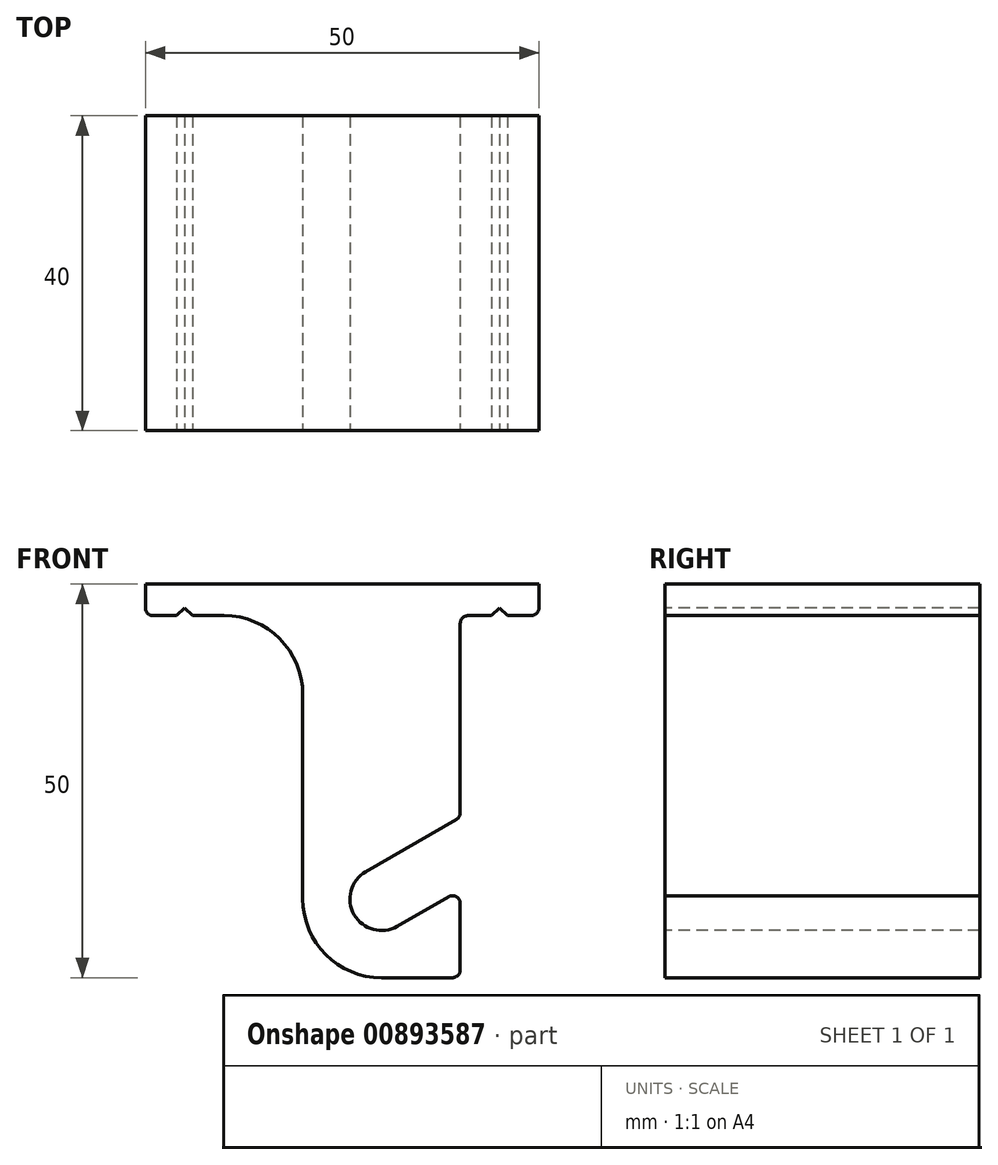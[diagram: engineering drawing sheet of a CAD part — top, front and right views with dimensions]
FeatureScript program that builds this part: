
annotation { "Feature Type Name" : "Feature", "Feature Type Description" : "" }
export const myFeature = defineFeature(function(context is Context, id is Id, definition is map)
    precondition{}
    {
        {
            var Q0;
            Q0=qCreatedBy(makeId("Front.planeOp"),FACE);
            var sketch = newSketch(context, id + "F0", { "sketchPlane" : qUnion([Q0])});
            skLineSegment(sketch, "E0", {"start": v(-50, 0) * mm, "end": v(0, 0) * mm});
            skLineSegment(sketch, "E1", {"start": v(-10.5, -29.9) * mm, "end": v(-22, -36.54) * mm});
            skArc(sketch, "E2", {"start": v(-22, -36.54) * mm, "mid": v(-23.46, -42) * mm, "end": v(-18, -43.46) * mm});
            skLineSegment(sketch, "E3", {"start": v(-18, -43.46) * mm, "end": v(-11.5, -39.71) * mm});
            skLineSegment(sketch, "E4", {"start": v(0, 0) * mm, "end": v(0, -3) * mm});
            skLineSegment(sketch, "E5", {"start": v(-1, -4) * mm, "end": v(-4, -4) * mm});
            skLineSegment(sketch, "E6", {"start": v(-10, -5) * mm, "end": v(-10, -29.03) * mm});
            skPoint(sketch, "E7.visualSharp", {"position": v(-10, -4) * mm});
            skArc(sketch, "E7.filletArc", {"start": v(-9, -4) * mm, "mid": v(-9.7, -4.3) * mm, "end": v(-10, -5) * mm});
            skLineSegment(sketch, "E8", {"start": v(-50, 0) * mm, "end": v(-50, -3) * mm});
            skLineSegment(sketch, "E9", {"start": v(-49, -4) * mm, "end": v(-46, -4) * mm});
            skArc(sketch, "E10", {"start": v(-30, -40) * mm, "mid": v(-27.07, -47.07) * mm, "end": v(-20, -50) * mm});
            skLineSegment(sketch, "E11", {"start": v(-20, -50) * mm, "end": v(-11, -50) * mm});
            skLineSegment(sketch, "E12", {"start": v(-10, -49) * mm, "end": v(-10, -40.58) * mm});
            skArc(sketch, "E13.filletArc", {"start": v(-10, -40.58) * mm, "mid": v(-10.5, -39.71) * mm, "end": v(-11.5, -39.71) * mm});
            skPoint(sketch, "E14.visualSharp", {"position": v(-10, -29.6) * mm});
            skArc(sketch, "E14.filletArc", {"start": v(-10.5, -29.9) * mm, "mid": v(-10.13, -29.53) * mm, "end": v(-10, -29.03) * mm});
            skPoint(sketch, "E15.visualSharp", {"position": v(-10, -50) * mm});
            skArc(sketch, "E15.filletArc", {"start": v(-11, -50) * mm, "mid": v(-10.3, -49.7) * mm, "end": v(-10, -49) * mm});
            skPoint(sketch, "E16.visualSharp", {"position": v(0, -4) * mm});
            skArc(sketch, "E16.filletArc", {"start": v(-1, -4) * mm, "mid": v(-0.3, -3.7) * mm, "end": v(0, -3) * mm});
            skPoint(sketch, "E17.visualSharp", {"position": v(-50, -4) * mm});
            skArc(sketch, "E17.filletArc", {"start": v(-50, -3) * mm, "mid": v(-49.7, -3.7) * mm, "end": v(-49, -4) * mm});
            skLineSegment(sketch, "E18.top", {"start": v(-1, -8) * mm, "end": v(-9, -8) * mm, "construction": true});
            skLineSegment(sketch, "E18.left", {"start": v(-1, -4) * mm, "end": v(-1, -8) * mm, "construction": true});
            skLineSegment(sketch, "E18.right", {"start": v(-9, -4) * mm, "end": v(-9, -8) * mm, "construction": true});
            skLineSegment(sketch, "E19", {"start": v(-6, -4) * mm, "end": v(-5, -3) * mm});
            skLineSegment(sketch, "E20", {"start": v(-5, -3) * mm, "end": v(-4, -4) * mm});
            skLineSegment(sketch, "E21.trimOffspring", {"start": v(-6, -4) * mm, "end": v(-9, -4) * mm});
            skLineSegment(sketch, "E22", {"start": v(-30, -40) * mm, "end": v(-30, -14) * mm});
            skPoint(sketch, "E23.visualSharp", {"position": v(-30, -4) * mm});
            skArc(sketch, "E23.filletArc", {"start": v(-30, -14) * mm, "mid": v(-32.93, -6.93) * mm, "end": v(-40, -4) * mm});
            skLineSegment(sketch, "E24", {"start": v(-46, -4) * mm, "end": v(-45, -3) * mm});
            skLineSegment(sketch, "E25", {"start": v(-45, -3) * mm, "end": v(-44, -4) * mm});
            skLineSegment(sketch, "E26.trimOffspring", {"start": v(-44, -4) * mm, "end": v(-40, -4) * mm});
            skSolve(sketch);
        }
        {
            var Q0;
            Q0=qSketchRegion(id+"F0",true);
            extrude(context, id + "F1", {"entities" : qUnion([Q0]), "oppositeDirection" : true, "depth" : 40 * mm, "offsetDistance" : 25 * mm});
        }
    });
